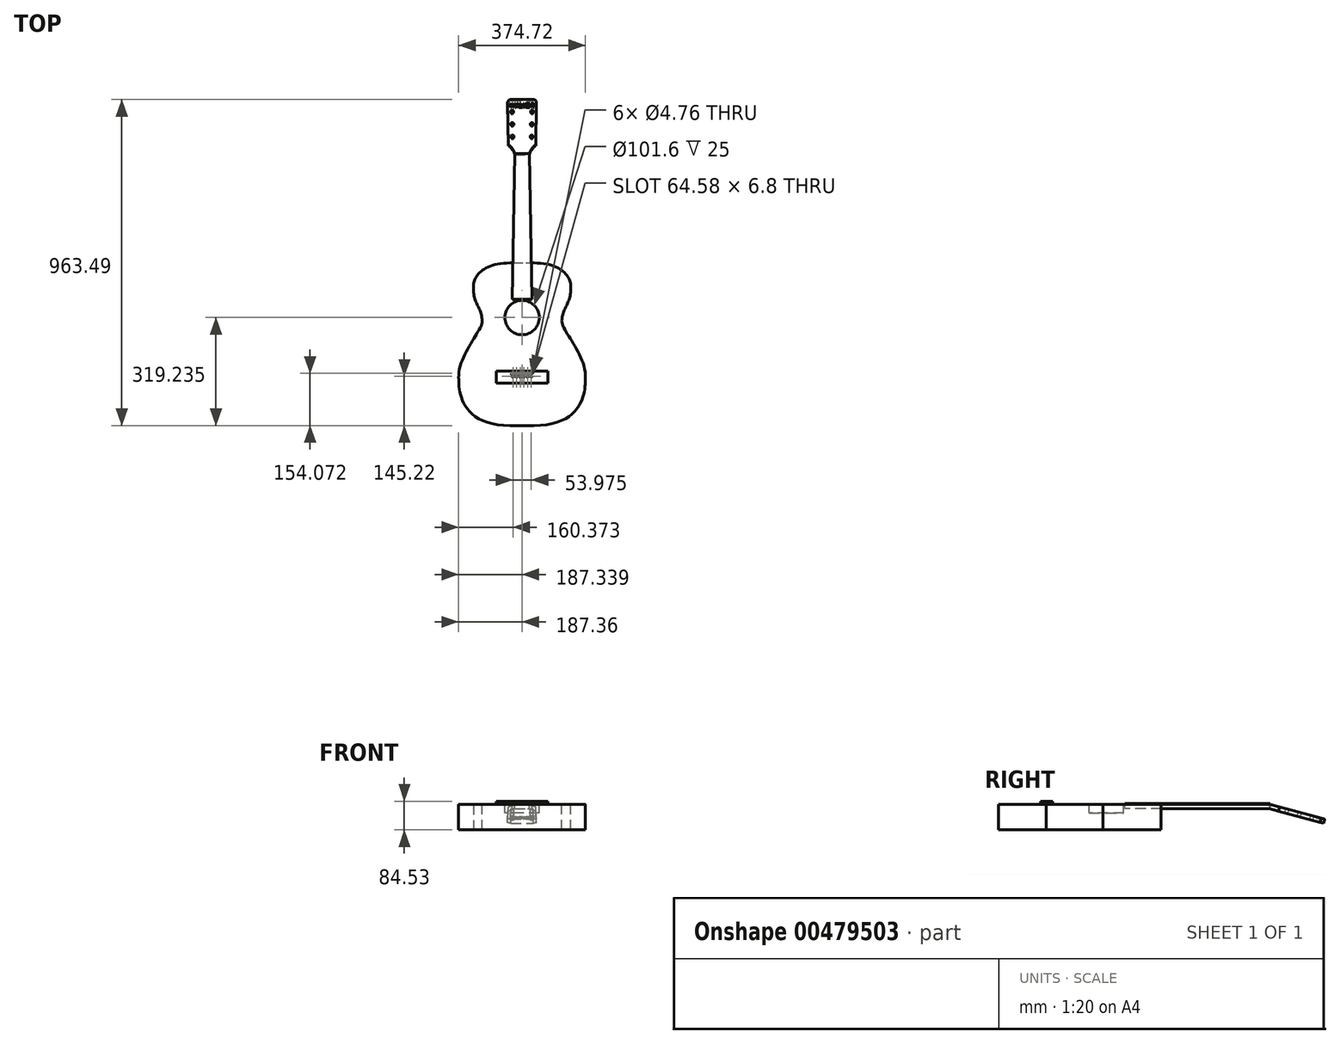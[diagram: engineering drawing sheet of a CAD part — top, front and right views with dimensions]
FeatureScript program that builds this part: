
annotation { "Feature Type Name" : "Feature", "Feature Type Description" : "" }
export const myFeature = defineFeature(function(context is Context, id is Id, definition is map)
    precondition{}
    {
        {
            var Q0;
            Q0=qCreatedBy(makeId("Top.planeOp"),FACE);
            var sketch = newSketch(context, id + "F0", { "sketchPlane" : qUnion([Q0])});
            skLineSegment(sketch, "E0", {"start": v(0, 411) * mm, "end": v(144, 411) * mm, "construction": true});
            skLineSegment(sketch, "E1", {"start": v(0, 309) * mm, "end": v(117.5, 309) * mm, "construction": true});
            skLineSegment(sketch, "E2", {"start": v(0, 141.2) * mm, "end": v(187.3, 141.2) * mm, "construction": true});
            skLineSegment(sketch, "E3", {"start": v(0, 309) * mm, "end": v(0, 411) * mm, "construction": true});
            skLineSegment(sketch, "E4", {"start": v(0, 309) * mm, "end": v(0, 141.2) * mm, "construction": true});
            skFitSpline(sketch, "E5", {"points": [v(35, 480.5) * mm, v(144, 411) * mm], "startDerivative": vector(238.36, -1.43) * mm, "endDerivative": vector(2.4, -95.1) * mm});
            skFitSpline(sketch, "E6", {"points": [v(144, 411) * mm, v(117.5, 309) * mm], "startDerivative": vector(4.95, -150.7) * mm, "endDerivative": vector(-8.54, -130.58) * mm});
            skFitSpline(sketch, "E7", {"points": [v(117.5, 309) * mm, v(187.3, 141.2) * mm], "startDerivative": vector(3.6, -94.3) * mm, "endDerivative": vector(-7, -199.9) * mm});
            skFitSpline(sketch, "E8", {"points": [v(187.3, 141.2) * mm, v(35, 0) * mm], "startDerivative": vector(-1.47, -70.03) * mm, "endDerivative": vector(-470.9, 0) * mm});
            skLineSegment(sketch, "E9.MirrorCS", {"start": v(0, 411) * mm, "end": v(-144, 411) * mm, "construction": true});
            skFitSpline(sketch, "E10.MirrorCS", {"points": [v(-187.3, 141.2) * mm, v(-35, 0) * mm], "startDerivative": vector(1.47, -70.03) * mm, "endDerivative": vector(470.9, 0) * mm});
            skFitSpline(sketch, "E11.MirrorCS", {"points": [v(-117.5, 309) * mm, v(-187.3, 141.2) * mm], "startDerivative": vector(-3.6, -94.3) * mm, "endDerivative": vector(7, -199.9) * mm});
            skFitSpline(sketch, "E12.MirrorCS", {"points": [v(-144, 411) * mm, v(-117.5, 309) * mm], "startDerivative": vector(-4.95, -150.7) * mm, "endDerivative": vector(8.54, -130.58) * mm});
            skFitSpline(sketch, "E13.MirrorCS", {"points": [v(-35, 480.5) * mm, v(-144, 411) * mm], "startDerivative": vector(-238.36, -1.43) * mm, "endDerivative": vector(-2.4, -95.1) * mm});
            skLineSegment(sketch, "E14.MirrorCS", {"start": v(0, 141.2) * mm, "end": v(-187.3, 141.2) * mm, "construction": true});
            skLineSegment(sketch, "E15.MirrorCS", {"start": v(0, 309) * mm, "end": v(-117.5, 309) * mm, "construction": true});
            skLineSegment(sketch, "E16", {"start": v(0, 411) * mm, "end": v(0, 480.5) * mm, "construction": true});
            skLineSegment(sketch, "E17", {"start": v(0, 480.5) * mm, "end": v(35, 480.5) * mm});
            skLineSegment(sketch, "E18.MirrorCS", {"start": v(0, 480.5) * mm, "end": v(-35, 480.5) * mm});
            skLineSegment(sketch, "E19", {"start": v(0, 0) * mm, "end": v(0, 141.2) * mm, "construction": true});
            skLineSegment(sketch, "E20", {"start": v(0, 0) * mm, "end": v(35, 0) * mm});
            skLineSegment(sketch, "E21.MirrorCS", {"start": v(0, 0) * mm, "end": v(-35, 0) * mm});
            skSolve(sketch);
        }
        {
            var Q0;
            Q0=qCreatedBy(makeId("Top.planeOp"),FACE);
            var sketch = newSketch(context, id + "F1", { "sketchPlane" : qUnion([Q0])});
            skLineSegment(sketch, "E22", {"start": v(0, 117.28) * mm, "end": v(0, 803.08) * mm, "construction": true});
            skPoint(sketch, "E23", {"position": v(0, 157.92) * mm});
            skPoint(sketch, "E24", {"position": v(0, 145.22) * mm});
            skLineSegment(sketch, "E25", {"start": v(0, 145.22) * mm, "end": v(26.99, 145.22) * mm});
            skLineSegment(sketch, "E26.MirrorCS", {"start": v(0, 145.22) * mm, "end": v(-26.99, 145.22) * mm});
            skLineSegment(sketch, "E27", {"start": v(0, 803.08) * mm, "end": v(21.43, 803.08) * mm});
            skLineSegment(sketch, "E28.MirrorCS", {"start": v(0, 803.08) * mm, "end": v(-21.43, 803.08) * mm});
            skPoint(sketch, "E29", {"position": v(18.26, 803.08) * mm});
            skPoint(sketch, "E30.MirrorP", {"position": v(-18.26, 803.08) * mm});
            skLineSegment(sketch, "E31", {"start": v(-18.26, 803.08) * mm, "end": v(-26.99, 145.22) * mm, "construction": true});
            skLineSegment(sketch, "E32", {"start": v(26.99, 145.22) * mm, "end": v(18.26, 803.08) * mm, "construction": true});
            skPoint(sketch, "E33", {"position": v(0, 480.5) * mm});
            skLineSegment(sketch, "E34", {"start": v(0, 480.5) * mm, "end": v(22.54, 480.5) * mm});
            skLineSegment(sketch, "E35", {"start": v(22.54, 480.5) * mm, "end": v(27.3, 480.56) * mm});
            skLineSegment(sketch, "E36.MirrorCS", {"start": v(0, 480.5) * mm, "end": v(-22.54, 480.5) * mm});
            skLineSegment(sketch, "E37.MirrorCS", {"start": v(-22.54, 480.5) * mm, "end": v(-27.3, 480.56) * mm});
            skPoint(sketch, "E38", {"position": v(0, 373.21) * mm});
            skPoint(sketch, "E39", {"position": v(0, 319.24) * mm});
            skCircle(sketch, "E40", {"center": v(0, 319.24) * mm, "radius": 50.8 * mm});
            skPoint(sketch, "E41", {"position": v(0, 370.04) * mm});
            skLineSegment(sketch, "E42", {"start": v(21.43, 803.08) * mm, "end": v(27.3, 480.56) * mm});
            skLineSegment(sketch, "E43", {"start": v(27.3, 480.56) * mm, "end": v(29.25, 373.21) * mm});
            skLineSegment(sketch, "E44", {"start": v(0, 373.21) * mm, "end": v(29.25, 373.21) * mm});
            skLineSegment(sketch, "E45.MirrorCS", {"start": v(-21.43, 803.08) * mm, "end": v(-27.3, 480.56) * mm});
            skLineSegment(sketch, "E46.MirrorCS", {"start": v(-27.3, 480.56) * mm, "end": v(-29.25, 373.21) * mm});
            skLineSegment(sketch, "E47.MirrorCS", {"start": v(-29.25, 373.21) * mm, "end": v(0, 373.21) * mm});
            skPoint(sketch, "E48", {"position": v(5.4, 145.22) * mm});
            skPoint(sketch, "E49", {"position": v(16.2, 145.22) * mm});
            skPoint(sketch, "E50.MirrorP", {"position": v(-5.4, 145.22) * mm});
            skPoint(sketch, "E51.MirrorP", {"position": v(-16.2, 145.22) * mm});
            skPoint(sketch, "E52", {"position": v(26.85, 155.66) * mm});
            skPoint(sketch, "E53", {"position": v(-26.9, 152.48) * mm});
            skLineSegment(sketch, "E54", {"start": v(-26.9, 152.48) * mm, "end": v(26.85, 155.66) * mm});
            skSolve(sketch);
        }
        {
            var Q0;
            Q0=qCreatedBy(makeId("Top.planeOp"),FACE);
            var sketch = newSketch(context, id + "F2", { "sketchPlane" : qUnion([Q0])});
            skPoint(sketch, "E55.0", {"position": v(-26.9, 152.48) * mm});
            skPoint(sketch, "E55.1", {"position": v(26.85, 155.66) * mm});
            skPoint(sketch, "E55.2", {"position": v(-5.4, 145.22) * mm});
            skPoint(sketch, "E55.3", {"position": v(-26.99, 145.22) * mm});
            skPoint(sketch, "E55.4", {"position": v(-16.2, 145.22) * mm});
            skPoint(sketch, "E55.5", {"position": v(5.4, 145.22) * mm});
            skPoint(sketch, "E55.6", {"position": v(16.2, 145.22) * mm});
            skPoint(sketch, "E55.7", {"position": v(26.99, 145.22) * mm});
            skPoint(sketch, "E56.0", {"position": v(0, 145.22) * mm});
            skLineSegment(sketch, "E57", {"start": v(-26.9, 152.48) * mm, "end": v(26.85, 155.66) * mm, "construction": true});
            skLineSegment(sketch, "E58", {"start": v(-26.9, 152.48) * mm, "end": v(-26.98, 154.07) * mm, "construction": true});
            skLineSegment(sketch, "E59.MirrorCS", {"start": v(-26.9, 152.48) * mm, "end": v(-26.8, 150.9) * mm, "construction": true});
            skLineSegment(sketch, "E60", {"start": v(-0.02, 154.07) * mm, "end": v(-0.17, 156.52) * mm, "construction": true});
            skLineSegment(sketch, "E61.MirrorCS", {"start": v(26.85, 155.66) * mm, "end": v(26.76, 157.24) * mm, "construction": true});
            skLineSegment(sketch, "E62.MirrorCS", {"start": v(26.85, 155.66) * mm, "end": v(26.94, 154.07) * mm, "construction": true});
            skLineSegment(sketch, "E63", {"start": v(-26.98, 154.07) * mm, "end": v(26.76, 157.24) * mm});
            skLineSegment(sketch, "E64", {"start": v(26.94, 154.07) * mm, "end": v(-26.8, 150.9) * mm});
            skLineSegment(sketch, "E65", {"start": v(-26.98, 154.07) * mm, "end": v(-30.82, 153.84) * mm});
            skLineSegment(sketch, "E66", {"start": v(-26.8, 150.9) * mm, "end": v(-30.63, 150.67) * mm});
            skArc(sketch, "E67", {"start": v(-30.82, 153.84) * mm, "mid": v(-32.31, 152.16) * mm, "end": v(-30.63, 150.67) * mm});
            skLineSegment(sketch, "E68.MirrorCS", {"start": v(26.76, 157.24) * mm, "end": v(30.6, 157.47) * mm});
            skLineSegment(sketch, "E69.MirrorCS", {"start": v(26.94, 154.07) * mm, "end": v(30.78, 154.3) * mm});
            skArc(sketch, "E70.MirrorCS", {"start": v(30.6, 157.47) * mm, "mid": v(32.27, 155.98) * mm, "end": v(30.78, 154.3) * mm});
            skLineSegment(sketch, "E71.0", {"start": v(0, 117.28) * mm, "end": v(0, 803.08) * mm, "construction": true});
            skCircle(sketch, "E72", {"center": v(26.99, 145.22) * mm, "radius": 2.38 * mm});
            skCircle(sketch, "E73", {"center": v(16.2, 145.22) * mm, "radius": 2.38 * mm});
            skCircle(sketch, "E74", {"center": v(5.4, 145.22) * mm, "radius": 2.38 * mm});
            skCircle(sketch, "E75.MirrorC", {"center": v(-5.4, 145.22) * mm, "radius": 2.38 * mm});
            skCircle(sketch, "E76.MirrorC", {"center": v(-16.2, 145.22) * mm, "radius": 2.38 * mm});
            skCircle(sketch, "E77.MirrorC", {"center": v(-26.99, 145.22) * mm, "radius": 2.38 * mm});
            skLineSegment(sketch, "E78", {"start": v(0, 160.42) * mm, "end": v(76.2, 160.42) * mm});
            skLineSegment(sketch, "E79", {"start": v(76.2, 160.42) * mm, "end": v(76.2, 124.86) * mm});
            skLineSegment(sketch, "E80", {"start": v(76.2, 124.86) * mm, "end": v(0, 124.86) * mm});
            skLineSegment(sketch, "E81.MirrorCS", {"start": v(0, 160.42) * mm, "end": v(-76.2, 160.42) * mm});
            skLineSegment(sketch, "E82.MirrorCS", {"start": v(-76.2, 160.42) * mm, "end": v(-76.2, 124.86) * mm});
            skLineSegment(sketch, "E83.MirrorCS", {"start": v(-76.2, 124.86) * mm, "end": v(0, 124.86) * mm});
            skSolve(sketch);
        }
        {
            var Q0;
            Q0=qCreatedBy(makeId("Right.planeOp"),FACE);
            var sketch = newSketch(context, id + "F3", { "sketchPlane" : qUnion([Q0])});
            skPoint(sketch, "E84.0", {"position": v(803.08, 0) * mm});
            skLineSegment(sketch, "E85", {"start": v(803.08, 0) * mm, "end": v(744.3, 0) * mm, "construction": true});
            skLineSegment(sketch, "E86", {"start": v(803.08, 0) * mm, "end": v(892.01, -23.83) * mm, "construction": true});
            skSolve(sketch);
        }
        {
            var Q0;
            Q0=sQuery(id+"F1.wireOp",VERTEX,"E29");
            var Q1;
            Q1=sQuery(id+"F1.wireOp",VERTEX,"E30.MirrorP");
            var Q2;
            Q2=sQuery(id+"F3.wireOp",VERTEX,"E86.end");
            cPlane(context, id + "F4", {"entities" : qUnion([Q0, Q1, Q2]), "cplaneType" : CPlaneType.THREE_POINT, "offset" : 25 * mm, "width" : 150 * mm, "height" : 150 * mm});
        }
        {
            var Q0;
            Q0=qCreatedBy(id+"F4.planeOp",FACE);
            var sketch = newSketch(context, id + "F5", { "sketchPlane" : qUnion([Q0])});
            skPoint(sketch, "E87.0", {"position": v(0, 775.72) * mm});
            skLineSegment(sketch, "E88", {"start": v(0, 775.72) * mm, "end": v(0, 953.52) * mm, "construction": true});
            skLineSegment(sketch, "E89", {"start": v(0, 775.72) * mm, "end": v(50.8, 775.72) * mm, "construction": true});
            skLineSegment(sketch, "E90.MirrorCS", {"start": v(0, 775.72) * mm, "end": v(-50.8, 775.72) * mm, "construction": true});
            skLineSegment(sketch, "E91", {"start": v(50.8, 775.72) * mm, "end": v(50.8, 953.52) * mm, "construction": true});
            skLineSegment(sketch, "E92", {"start": v(50.8, 953.52) * mm, "end": v(0, 953.52) * mm, "construction": true});
            skLineSegment(sketch, "E93.MirrorCS", {"start": v(-50.8, 953.52) * mm, "end": v(0, 953.52) * mm, "construction": true});
            skLineSegment(sketch, "E94.MirrorCS", {"start": v(-50.8, 775.72) * mm, "end": v(-50.8, 953.52) * mm, "construction": true});
            skPoint(sketch, "E95.1", {"position": v(21.43, 775.72) * mm});
            skPoint(sketch, "E96.MirrorP", {"position": v(-21.43, 775.72) * mm});
            skPoint(sketch, "E97", {"position": v(0, 828.1) * mm});
            skPoint(sketch, "E98", {"position": v(0, 866.2) * mm});
            skPoint(sketch, "E99", {"position": v(0, 904.3) * mm});
            skLineSegment(sketch, "E100", {"start": v(0, 941.78) * mm, "end": v(33.63, 941.78) * mm});
            skLineSegment(sketch, "E101", {"start": v(42.54, 932.71) * mm, "end": v(40.47, 803.74) * mm});
            skCircle(sketch, "E102", {"center": v(28.36, 828.1) * mm, "radius": 4.76 * mm});
            skCircle(sketch, "E103", {"center": v(28.97, 866.2) * mm, "radius": 4.76 * mm});
            skCircle(sketch, "E104", {"center": v(29.59, 904.3) * mm, "radius": 4.76 * mm});
            skLineSegment(sketch, "E105.MirrorCS", {"start": v(0, 941.78) * mm, "end": v(-33.63, 941.78) * mm});
            skLineSegment(sketch, "E106.MirrorCS", {"start": v(-42.54, 932.71) * mm, "end": v(-40.47, 803.74) * mm});
            skCircle(sketch, "E107.MirrorC", {"center": v(-29.59, 904.3) * mm, "radius": 4.76 * mm});
            skCircle(sketch, "E108.MirrorC", {"center": v(-28.97, 866.2) * mm, "radius": 4.76 * mm});
            skCircle(sketch, "E109.MirrorC", {"center": v(-28.36, 828.1) * mm, "radius": 4.76 * mm});
            skArc(sketch, "E110", {"start": v(40.47, 803.74) * mm, "mid": v(28.6, 791.32) * mm, "end": v(21.43, 775.72) * mm});
            skArc(sketch, "E111.MirrorCS", {"start": v(-40.47, 803.74) * mm, "mid": v(-28.6, 791.32) * mm, "end": v(-21.43, 775.72) * mm});
            skArc(sketch, "E112", {"start": v(42.53, 931.78) * mm, "mid": v(39.85, 938.98) * mm, "end": v(32.7, 941.78) * mm});
            skPoint(sketch, "E113.orphan", {"position": v(42.7, 941.78) * mm});
            skArc(sketch, "E114.MirrorCS", {"start": v(-42.53, 931.78) * mm, "mid": v(-39.85, 938.98) * mm, "end": v(-32.7, 941.78) * mm});
            skPoint(sketch, "E115.orphan", {"position": v(-42.7, 941.78) * mm});
            skLineSegment(sketch, "E116", {"start": v(-21.43, 775.72) * mm, "end": v(21.43, 775.72) * mm});
            skSolve(sketch);
        }
        {
            var Q0;
            Q0=qCreatedBy(id+"F4.planeOp",FACE);
            var sketch = newSketch(context, id + "F6", { "sketchPlane" : qUnion([Q0])});
            skLineSegment(sketch, "E117.0", {"start": v(0, 775.72) * mm, "end": v(0, 953.52) * mm, "construction": true});
            skText(sketch, "E118", { "text": "WALKER", "fontName": "OpenSans-Regular.ttf"});
            const initialGuessF6  = {"E118": [-0.03723, 0.9172, 1, 0, 0.0137]};
            skSetInitialGuess(sketch, initialGuessF6);
            skSolve(sketch);
        }
        {
            var Q0;
            Q0 = qSketchRegion(id + "F5", true);
            extrude(context, id + "F7", {"entities" : qUnion([Q0]), "oppositeDirection" : true, "depth" : 12.5 * mm, "offsetDistance" : 25 * mm});
        }
        {
            var Q0;
            Q0 = qSketchRegion(id + "F6", true);
            extrude(context, id + "F8", {"entities" : qUnion([Q0]), "operationType" : NewBodyOperationType.REMOVE, "oppositeDirection" : true, "depth" : 3.17 * mm, "offsetDistance" : 25 * mm});
        }
        {
            var Q0;
            Q0=makeQuery(id+"F1.imprint","IMPRINT",FACE,{"disambiguationData":[TD([[makeQuery(id+"F1.imprint","IMPRINT",EDGE,{"derivedFrom":sQuery(id+"F1.wireOp",EDGE,"E27")}),-1.0]])]});
            var Q1;
            Q1=makeQuery(id+"F1.imprint","IMPRINT",FACE,{"disambiguationData":[TD([[makeQuery(id+"F1.imprint","IMPRINT",EDGE,{"derivedFrom":sQuery(id+"F1.wireOp",EDGE,"E34")}),-1.0]])]});
            extrude(context, id + "F9", {"entities" : qUnion([Q0, Q1]), "depth" : 3.17 * mm, "offsetDistance" : 25 * mm});
        }
        {
            var Q0;
            Q0=makeQuery(id+"F1.imprint","IMPRINT",FACE,{"disambiguationData":[TD([[makeQuery(id+"F1.imprint","IMPRINT",EDGE,{"derivedFrom":sQuery(id+"F1.wireOp",EDGE,"E27")}),-1.0]])]});
            var Q1;
            Q1=makeQuery(id+"F1.imprint","IMPRINT",FACE,{"disambiguationData":[TD([[makeQuery(id+"F1.imprint","IMPRINT",EDGE,{"derivedFrom":sQuery(id+"F1.wireOp",EDGE,"E34")}),-1.0]])]});
            extrude(context, id + "F10", {"entities" : qUnion([Q0, Q1]), "oppositeDirection" : true, "depth" : 12.5 * mm, "offsetDistance" : 25 * mm});
        }
        {
            var Q0;
            Q0=makeQuery(id+"F0.imprint","IMPRINT",FACE,{"disambiguationData":[TD([[makeQuery(id+"F0.imprint","IMPRINT",EDGE,{"derivedFrom":sQuery(id+"F0.wireOp",EDGE,"E5")}),-1.0]])]});
            extrude(context, id + "F11", {"entities" : qUnion([Q0]), "oppositeDirection" : true, "depth" : 75 * mm, "offsetDistance" : 25 * mm});
        }
        {
            var Q0;
            Q0=makeQuery(id+"F1.imprint","IMPRINT",FACE,{"disambiguationData":[TD([[makeQuery(id+"F1.imprint","IMPRINT",EDGE,{"derivedFrom":sQuery(id+"F1.wireOp",EDGE,"E40")}),1.0]])]});
            extrude(context, id + "F12", {"entities" : qUnion([Q0]), "operationType" : NewBodyOperationType.REMOVE, "oppositeDirection" : true, "depth" : 25 * mm, "offsetDistance" : 25 * mm});
        }
        {
            var Q0;
            Q0=makeQuery(id+"F2.imprint","IMPRINT",FACE,{"disambiguationData":[TD([[makeQuery(id+"F2.imprint","IMPRINT",EDGE,{"derivedFrom":sQuery(id+"F2.wireOp",EDGE,"E63")}),1.0]])]});
            extrude(context, id + "F13", {"entities" : qUnion([Q0]), "depth" : 9.53 * mm, "offsetDistance" : 25 * mm});
        }
    });
